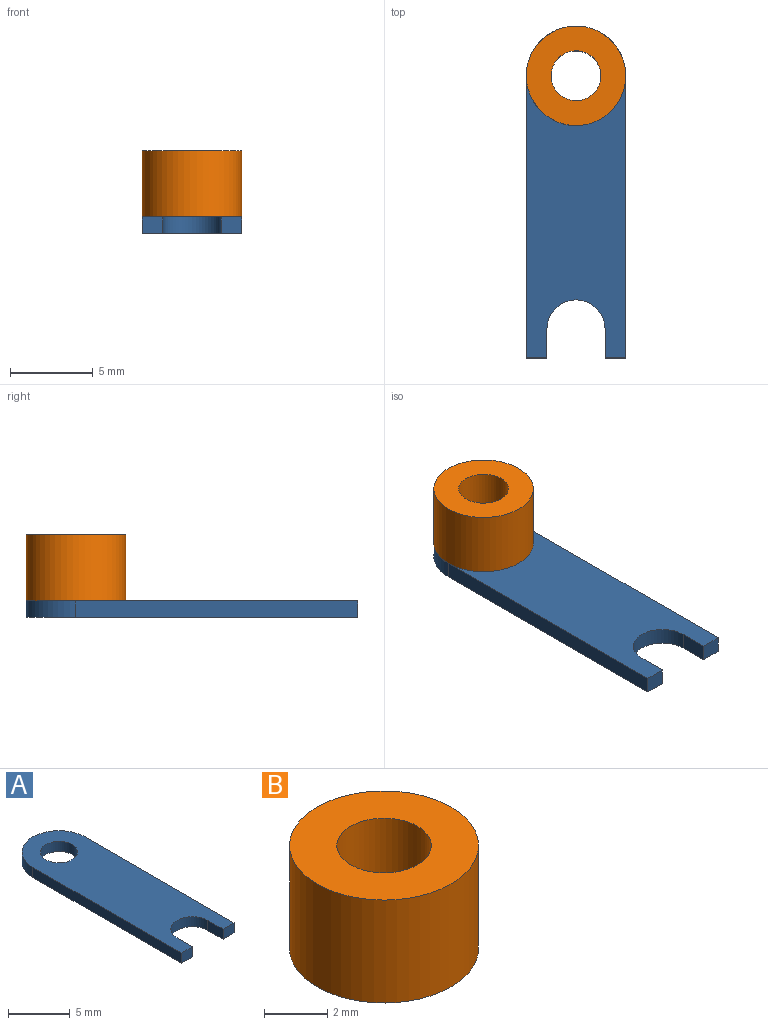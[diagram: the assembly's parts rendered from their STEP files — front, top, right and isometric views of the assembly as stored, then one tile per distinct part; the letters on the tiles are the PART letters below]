
ASSEMBLY  parts=2 mates=1
PART A: 11 faces, bbox 6x20x1 mm
  f0: plane 17x1mm, normal (1,0,0), area 17mm2, adj f1,f7,f8,f9
  f1: cylinder r=3mm len=6mm, axis (0,0,-1), area 9.4mm2, adj f0,f2,f8,f9
  f2: plane 17x1mm, normal (-1,0,0), area 17mm2, adj f1,f3,f8,f9
  f3: plane 1.25x1mm, normal (0,-1,0), area 1.3mm2, adj f2,f4,f8,f9
  f4: plane 1.75x1mm, normal (1,0,0), area 1.8mm2, adj f3,f5,f8,f9
  f5: cylinder r=1.75mm len=3.5mm, axis (0,0,-1), area 5.5mm2, adj f4,f6,f8,f9
  f6: plane 1.75x1mm, normal (-1,0,0), area 1.8mm2, adj f5,f7,f8,f9
  f7: plane 1.25x1mm, normal (0,-1,0), area 1.2mm2, adj f0,f6,f8,f9
  f8: plane 20x6mm, normal (0,0,1), area 98.1mm2, adj f0,f1,f2,f3,f4,f5,f6,f7
  f9: plane 20x6mm, normal (0,0,-1), area 98.1mm2, adj f0,f1,f2,f3,f4,f5,f6,f7
  f10: cylinder r=1.5mm len=3mm, axis (0,0,1), area 9.4mm2, adj f8,f9
PART B: 4 faces, bbox 6x6x4 mm
  f0: cylinder r=1.5mm len=4mm, axis (0,0,-1), area 37.7mm2, adj f2,f3
  f1: cylinder r=3mm len=6mm, axis (0,0,-1), area 75.4mm2, adj f2,f3
  f2: plane 6x6mm, normal (0,0,1), area 21.2mm2, adj f0,f1
  f3: plane 6x6mm, normal (0,0,-1), area 21.2mm2, adj f0,f1
PLACE A t=(3,-17,-1)mm
PLACE B at identity
MATE fastened A.f1 <-> B.f0  axis (0,0,1) through (0,0,0)mm
